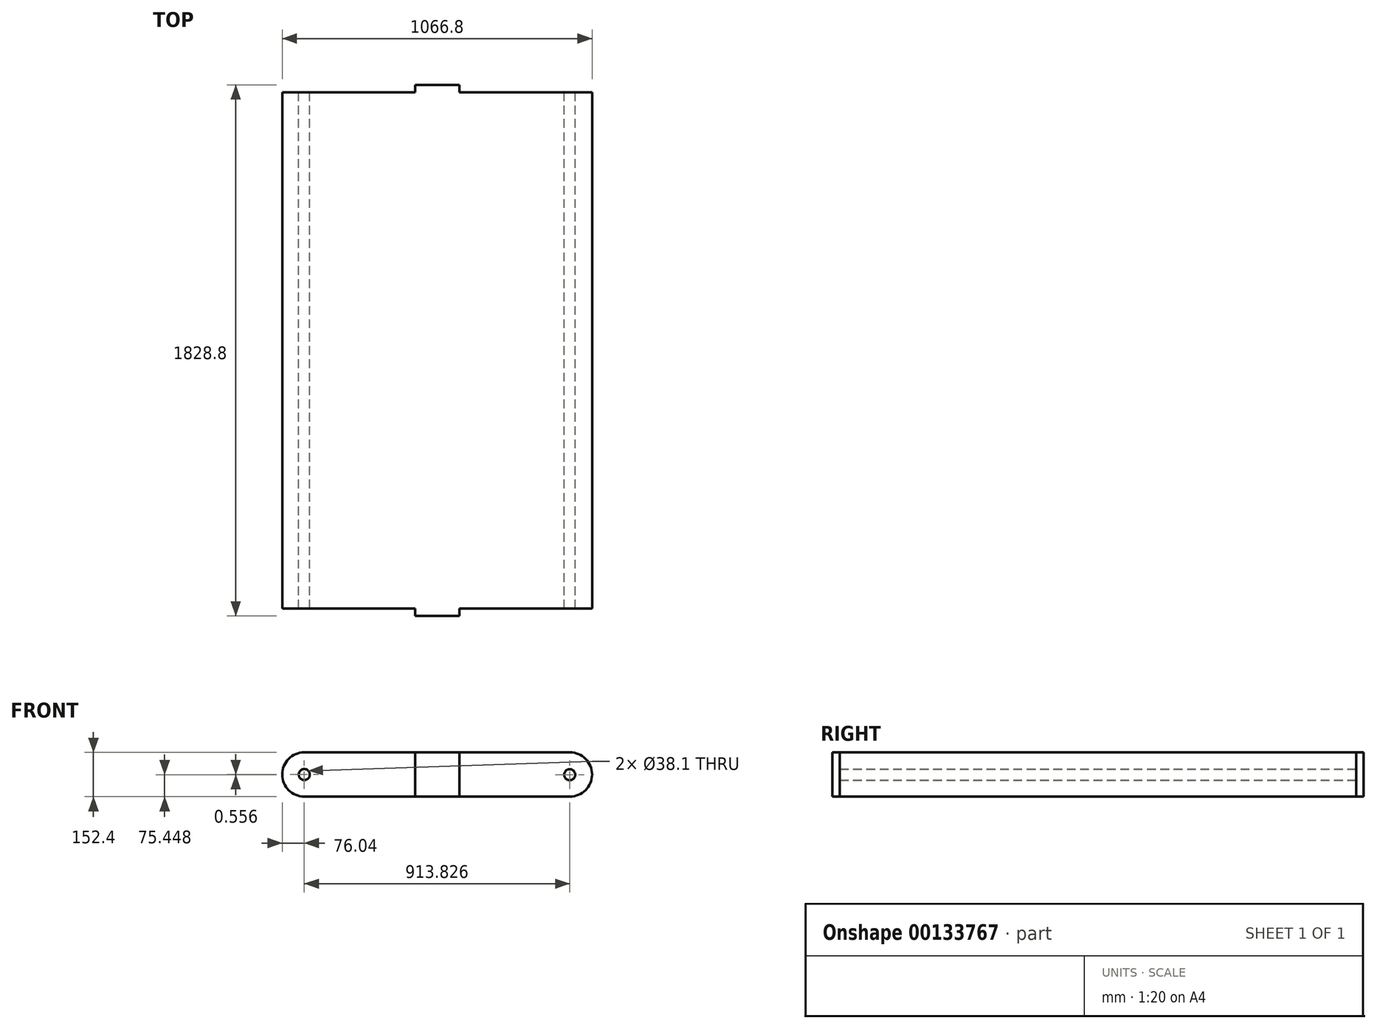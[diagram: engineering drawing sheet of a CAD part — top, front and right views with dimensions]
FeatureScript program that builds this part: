
annotation { "Feature Type Name" : "Feature", "Feature Type Description" : "" }
export const myFeature = defineFeature(function(context is Context, id is Id, definition is map)
    precondition{}
    {
        {
            var Q0;
            Q0=qCreatedBy(makeId("Front.planeOp"),FACE);
            var sketch = newSketch(context, id + "F0", { "sketchPlane" : qUnion([Q0])});
            skLineSegment(sketch, "E0", {"start": v(-105.97, 152.4) * mm, "end": v(808.43, 152.4) * mm});
            skArc(sketch, "E1", {"start": v(808.43, 0) * mm, "mid": v(884.63, 76.2) * mm, "end": v(808.43, 152.4) * mm});
            skLineSegment(sketch, "E2", {"start": v(808.43, 0) * mm, "end": v(-105.97, 0) * mm});
            skArc(sketch, "E3", {"start": v(-105.97, 152.4) * mm, "mid": v(-182.17, 76.2) * mm, "end": v(-105.97, 0) * mm});
            skSolve(sketch);
        }
        {
            var Q0;
            Q0=makeQuery(id+"F0.imprint","IMPRINT",FACE,{"disambiguationData":[TD([[makeQuery(id+"F0.imprint","IMPRINT",EDGE,{"derivedFrom":sQuery(id+"F0.wireOp",EDGE,"E0")}),-1.0]])]});
            var sketch = newSketch(context, id + "F1", { "sketchPlane" : qUnion([Q0])});
            skCircle(sketch, "E4", {"center": v(-106.13, 76) * mm, "radius": 19.05 * mm});
            skCircle(sketch, "E5", {"center": v(807.7, 75.45) * mm, "radius": 19.05 * mm});
            skSolve(sketch);
        }
        {
            var Q0;
            Q0=makeQuery(id+"F1.imprint","IMPRINT",FACE,{"disambiguationData":[TD([[makeQuery(id+"F1.imprint","IMPRINT",EDGE,{"derivedFrom":sQuery(id+"F1.wireOp",EDGE,"E4")}),-1.0]])]});
            extrude(context, id + "F2", {"entities" : qUnion([Q0]), "depth" : 1778 * mm});
        }
        {
            var Q0;
            Q0=makeQuery(id+"F2.opExtrude","CAP_FACE",FACE,{"disambiguationData":[OSD([sQuery(id+"F0.wireOp",EDGE,"E0"),sQuery(id+"F0.wireOp",EDGE,"E1"),sQuery(id+"F0.wireOp",EDGE,"E2"),sQuery(id+"F0.wireOp",EDGE,"E3"),sQuery(id+"F1.wireOp",EDGE,"E4"),sQuery(id+"F1.wireOp",EDGE,"E5")])],"isStart":false});
            var sketch = newSketch(context, id + "F3", { "sketchPlane" : qUnion([Q0])});
            skLineSegment(sketch, "E6", {"start": v(351.23, 152.4) * mm, "end": v(427.43, 152.4) * mm});
            skLineSegment(sketch, "E7", {"start": v(427.43, 152.4) * mm, "end": v(427.43, 0) * mm});
            skLineSegment(sketch, "E8", {"start": v(427.43, 0) * mm, "end": v(275.03, 0) * mm});
            skLineSegment(sketch, "E9", {"start": v(275.03, 0) * mm, "end": v(275.03, 152.4) * mm});
            skLineSegment(sketch, "E10", {"start": v(275.03, 152.4) * mm, "end": v(351.23, 152.4) * mm});
            skSolve(sketch);
        }
        {
            var Q0;
            Q0=makeQuery(id+"F3.imprint","IMPRINT",FACE,{"disambiguationData":[TD([[makeQuery(id+"F3.imprint","IMPRINT",EDGE,{"derivedFrom":sQuery(id+"F3.wireOp",EDGE,"E6")}),-1.0]])]});
            extrude(context, id + "F4", {"entities" : qUnion([Q0]), "operationType" : NewBodyOperationType.ADD, "depth" : 25.4 * mm});
        }
        {
            var Q0;
            Q0=makeQuery(id+"F0.imprint","IMPRINT",FACE,{"disambiguationData":[TD([[makeQuery(id+"F0.imprint","IMPRINT",EDGE,{"derivedFrom":sQuery(id+"F0.wireOp",EDGE,"E0")}),-1.0]])]});
            var sketch = newSketch(context, id + "F5", { "sketchPlane" : qUnion([Q0])});
            skLineSegment(sketch, "E11", {"start": v(427.43, 153) * mm, "end": v(275.03, 153) * mm});
            skLineSegment(sketch, "E12", {"start": v(275.03, 0) * mm, "end": v(275.03, 153) * mm});
            skLineSegment(sketch, "E13", {"start": v(427.43, 0) * mm, "end": v(275.03, 0) * mm});
            skLineSegment(sketch, "E14", {"start": v(427.43, 153) * mm, "end": v(427.43, 0) * mm});
            skSolve(sketch);
        }
        {
            var Q0;
            {var subQ0=sQuery(id+"F5.wireOp",EDGE,"E13");Q0=makeQuery(id+"F5.imprint","IMPRINT",FACE,{"disambiguationData":[TD([[makeQuery(id+"F5.imprint","IMPRINT",EDGE,{"derivedFrom":subQ0}),-1.0]])]});}
            extrude(context, id + "F6", {"entities" : qUnion([Q0]), "operationType" : NewBodyOperationType.ADD, "oppositeDirection" : true, "depth" : 25.4 * mm});
        }
    });
